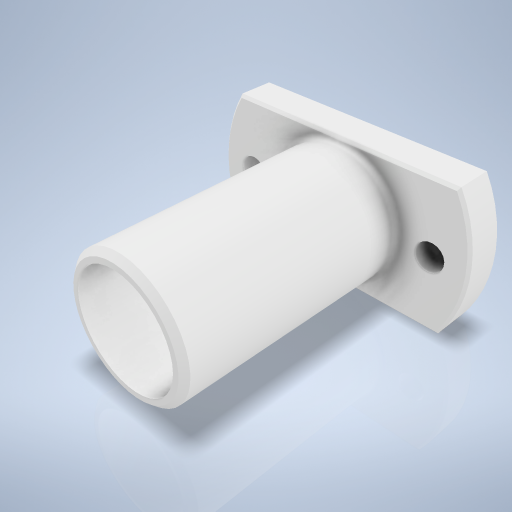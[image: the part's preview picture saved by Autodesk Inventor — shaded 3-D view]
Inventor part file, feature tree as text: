
AUTODESK INVENTOR PART (.ipt)
format: ipt  version: 2024.2 (Build 282272000, 272)  size: 307,200 bytes
history: native  units: mm
features: sketch x5, extrude x3, hole x2, chamfer x2, fillet x1, projected_geometry x1
ambient origin geometry x8: Origin, YZ Plane, XZ Plane, XY Plane, X Axis, Y Axis, Z Axis, Center Point
bodies: Volumenkörper1 (feature_tree)
feature tree (14):
  extrude  "Extrusion1"  Depth=6.5mm TaperAngle=0.0deg
  extrude  "Extrusion2"  Depth=12.5mm
  extrude  "Extrusion3"  Depth=23.0mm
  hole  "Bohrung1"  [1 undecoded]
  hole  "Bohrung2"  [1 undecoded]
  fillet  "Rundung1"  Radius=17.5mm
  chamfer  "Fasen1"  Distance=17.5mm
  chamfer  "Fasen2"  Distance=1.0mm
  sketch  "Skizze1"  dims[d0=48.0mm d1=6.5mm d2=0.0mm]
  sketch  "Skizze2"  dims[d3=12.5mm d4=12.5mm]
  projected_geometry  "Projizierte Kontur1"
  sketch  "Skizze3"  dims[d5=6.5mm d6=0.0mm d7=23.0mm]
  sketch  "Skizze4"  dims[d9=40.5mm d10=0.0mm]
  sketch  "Skizze5"  dims[d11=19.0mm d12=6.0mm d13=4.0mm d14=2.0mm d15=90.0deg d16=8.0mm d17=0.0mm d18=5.0mm d19=6.0mm d20=4.0mm d21=2.0mm d22=90.0deg d23=8.0mm d24=0.0mm d25=12.5mm d26=12.5mm d27=17.5mm d28=17.5mm d29=1.0mm d30=1.0mm d31=2.0mm d32=45.0deg d33=0.5mm d34=2.0mm d35=45.0deg]
note: 2 required parameter values undecoded (feature->parameter linkage not recoverable at this tier; creation-order binding heuristic only, values carry confidence <= 0.55)
